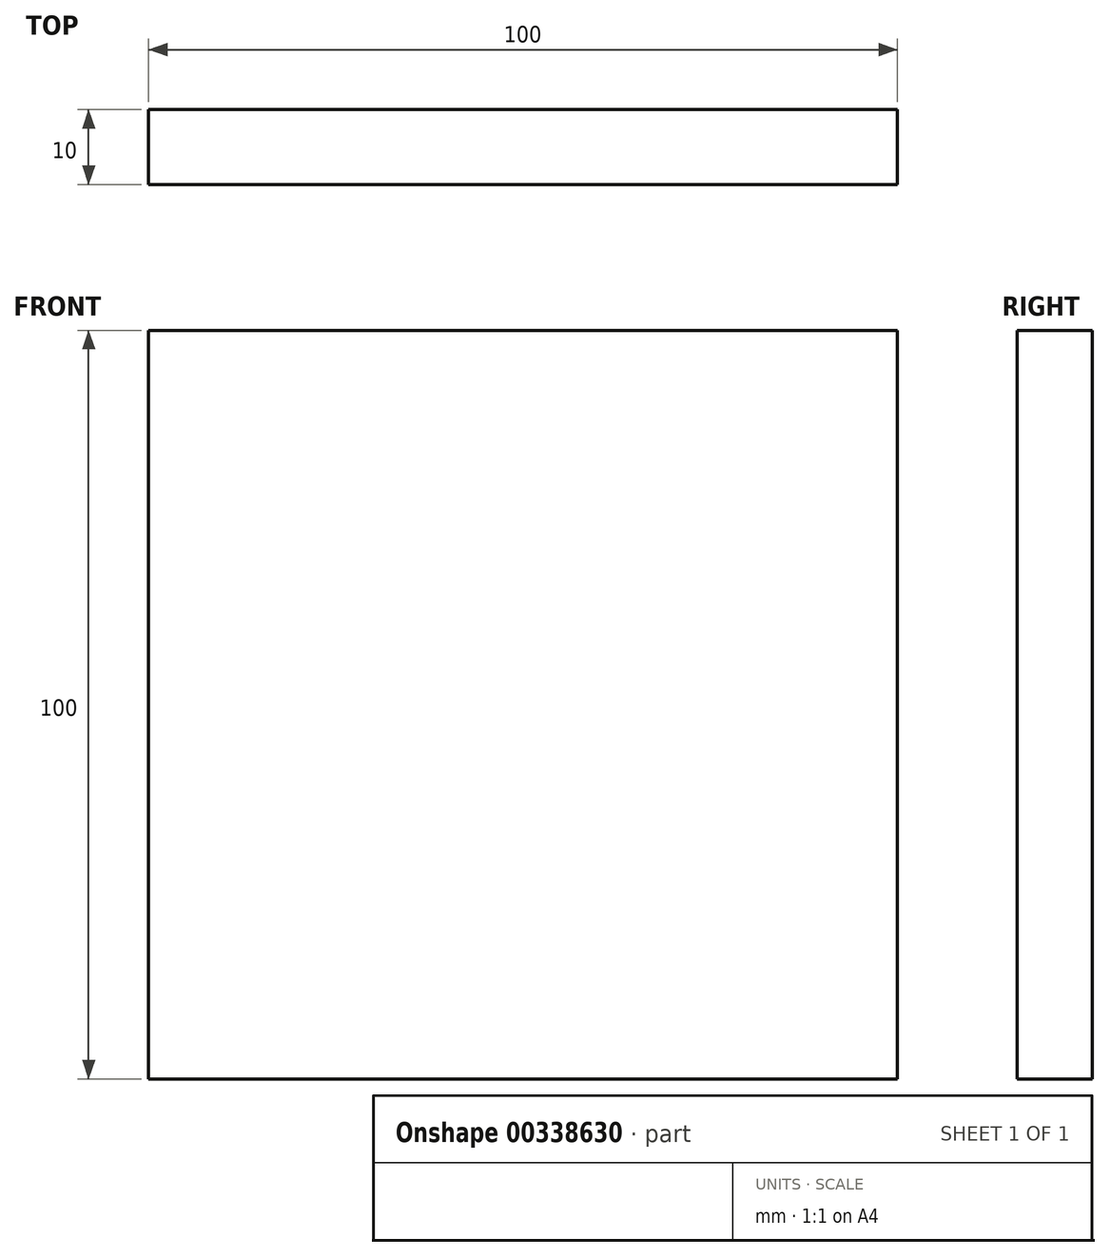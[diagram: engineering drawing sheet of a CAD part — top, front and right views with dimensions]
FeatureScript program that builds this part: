
annotation { "Feature Type Name" : "Feature", "Feature Type Description" : "" }
export const myFeature = defineFeature(function(context is Context, id is Id, definition is map)
    precondition{}
    {
        {
            var Q0;
            Q0=qCreatedBy(makeId("Front.planeOp"),FACE);
            var sketch = newSketch(context, id + "F0", { "sketchPlane" : qUnion([Q0])});
            skLineSegment(sketch, "E0.bottom", {"start": v(-50, 50) * mm, "end": v(50, 50) * mm});
            skLineSegment(sketch, "E0.top", {"start": v(-50, -50) * mm, "end": v(50, -50) * mm});
            skLineSegment(sketch, "E0.left", {"start": v(-50, 50) * mm, "end": v(-50, -50) * mm});
            skLineSegment(sketch, "E0.right", {"start": v(50, 50) * mm, "end": v(50, -50) * mm});
            skPoint(sketch, "E0.middle", {"position": v(0, 0) * mm});
            skSolve(sketch);
        }
        {
            var Q0;
            Q0 = qSketchRegion(id + "F0", true);
            extrude(context, id + "F1", {"entities" : qUnion([Q0]), "depth" : 10 * mm, "offsetDistance" : 25 * mm});
        }
    });
